# Revit family: quantum_310-4110
name_source: partatom
category: Leuchten
revit_build: Autodesk Revit 2016 (Build: 20190508_0715(x64)
units: mm (PartAtom-declared; Revit-internal decimal feet)

## family parameters
Basisbauteil = Fläche
Beim Laden mit Abzugskörper schneiden = Nein
Bemaßung runder Anschluss = Durchmesser verwenden
Gemeinsam genutzt = Nein
Lichtquelle = Nein
Raumberechnungspunkt = Nein
Teiletyp = Normal

## types (1)
- 310-4110-D01-H27 (1 x LED, 638.33 lm, 4.9 W, 2700K)
    Beschreibung = QUANTUM
    CIE Flux Codes = 44 75 94 100 65
    Color Rendering = 1A/90…99
    Color Temperature = 2700K
    Height = 120 mm
    Hersteller = Prolicht
    Lamp Light Flux = 638.33 lm
    Lamp Power = 4.9 W
    Lamp count = 1
    Lampe = 1 x LED
    Length = 317 mm
    Luminous efficacy = 85 lm/W
    ModVariant = Nein
    Modell = 310-4110
    Mounting Place = Ceiling
    Mounting Type = Surface mounted
    Number of Poles = 1
    OnlyDefault = Ja
    Power Factor = 1
    Product Name = QUANTUM
    Product group = Surface lights
    ProductGroupID = 331
    Protection Class = Protection class
    Protection Degree = Degree of protection
    RLX_Detail_Level = 1
    RlxData = <blob elided: 50473 chars, md5=deae80bb>
    Scheinlast = 59 VA
    Socket = socket
    Standby Power = 0 W
    System Light Flux = 4979 lm
    System Power = 59 W
    Typenbild = 310-4110.jpg
    Typenkommentare = DIFFUSER Opal (01),LED COLOUR DIR 2700 K (27)
    URL = http://relux.com
    VarID = 310-4110-d01-h27
    Voltage = 0 V
    Vorgabe-Ansicht = 1800 mm
    Weight = 0.00 kg
    Width = 150 mm

## geometry (parser evidence)
native form markers: Blend x4, Sweep x41
no freeform markers — native parametric forms only
